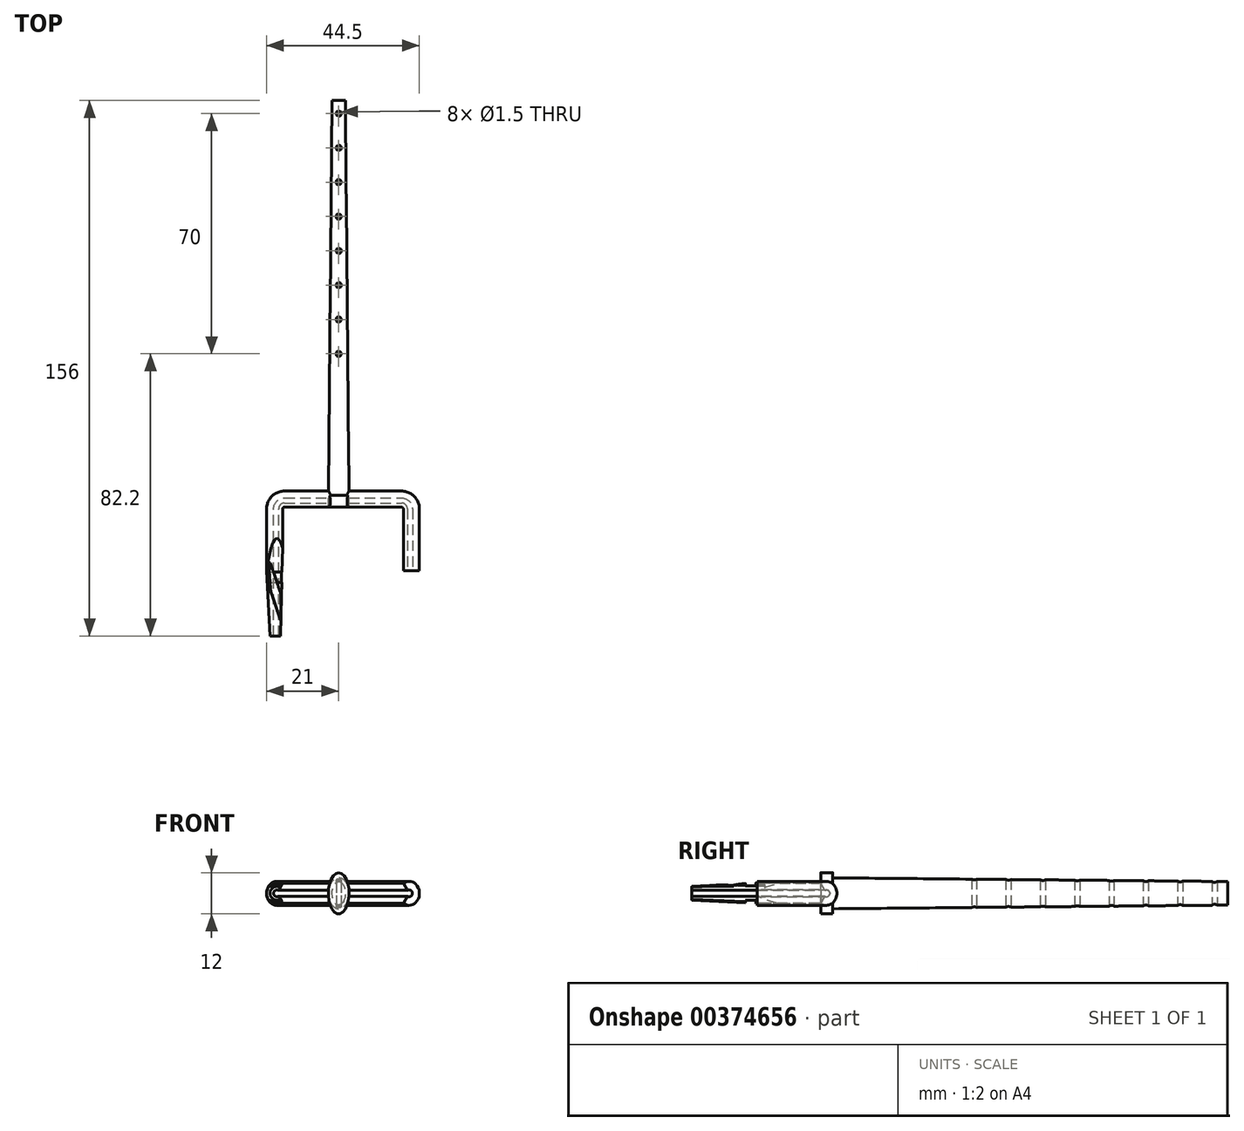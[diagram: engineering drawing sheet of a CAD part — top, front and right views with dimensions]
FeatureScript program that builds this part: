
annotation { "Feature Type Name" : "Feature", "Feature Type Description" : "" }
export const myFeature = defineFeature(function(context is Context, id is Id, definition is map)
    precondition{}
    {
        {
            var Q0;
            Q0=qCreatedBy(makeId("Front.planeOp"),FACE);
            var sketch = newSketch(context, id + "F0", { "sketchPlane" : qUnion([Q0])});
            skArc(sketch, "E0", {"start": v(0.49, 0.84) * mm, "mid": v(-0.97, 0) * mm, "end": v(0.49, -0.84) * mm});
            skLineSegment(sketch, "E1", {"start": v(0.49, 0.84) * mm, "end": v(1.68, 2.9) * mm});
            skLineSegment(sketch, "E2", {"start": v(0.49, -0.84) * mm, "end": v(1.68, -2.9) * mm});
            skEllipticalArc(sketch, "E3", {});
            const initialGuessF0  = {"E3": [0, 0, -1, 0, 0.003, 0.0035, 4.1196187055742195, 2.1635666016053645]};
            skSetInitialGuess(sketch, initialGuessF0);
            skSolve(sketch);
        }
        {
            var Q0;
            Q0=qCreatedBy(makeId("Top.planeOp"),FACE);
            var sketch = newSketch(context, id + "F1", { "sketchPlane" : qUnion([Q0])});
            skLineSegment(sketch, "E4", {"start": v(0, 0) * mm, "end": v(0, 37) * mm});
            skArc(sketch, "E5", {"start": v(0, 37) * mm, "mid": v(0.64, 38.56) * mm, "end": v(2.2, 39.2) * mm});
            skLineSegment(sketch, "E6", {"start": v(2.2, 39.2) * mm, "end": v(36.3, 39.2) * mm});
            skArc(sketch, "E7", {"start": v(38.5, 37) * mm, "mid": v(37.86, 38.56) * mm, "end": v(36.3, 39.2) * mm});
            skLineSegment(sketch, "E8", {"start": v(38.5, 37) * mm, "end": v(38.5, 19) * mm});
            skSolve(sketch);
        }
        {
            var Q0;
            Q0=qSketchRegion(id+"F0",true);
            var Q1;
            Q1=qConstructionFilter(qBodyType(qCreatedBy(id+"F0",EDGE),BodyType.WIRE),ConstructionObject.NO);
            var Q2;
            Q2=qConstructionFilter(qBodyType(qCreatedBy(id+"F1",EDGE),BodyType.WIRE),ConstructionObject.NO);
            sweep(context, id + "F2", {"profiles" : qUnion([Q0]), "surfaceProfiles" : qUnion([Q1]), "path" : qUnion([Q2])});
        }
        {
            var Q0;
            Q0=qCreatedBy(makeId("Right.planeOp"),FACE);
            var sketch = newSketch(context, id + "F3", { "sketchPlane" : qUnion([Q0])});
            skLineSegment(sketch, "E9", {"start": v(0, 2) * mm, "end": v(28.41, 3.5) * mm});
            skLineSegment(sketch, "E10", {"start": v(-1.87, 2) * mm, "end": v(0, 2) * mm});
            skLineSegment(sketch, "E11", {"start": v(-4.03, 0) * mm, "end": v(22.25, 0) * mm, "construction": true});
            skLineSegment(sketch, "E12", {"start": v(28.41, 3.5) * mm, "end": v(28.41, 8.2) * mm});
            skLineSegment(sketch, "E13", {"start": v(28.41, 8.2) * mm, "end": v(-1.87, 8.2) * mm});
            skLineSegment(sketch, "E14", {"start": v(-1.87, 8.2) * mm, "end": v(-1.87, 2) * mm});
            skSolve(sketch);
        }
        {
            var Q0;
            Q0=makeQuery(id+"F3.imprint","IMPRINT",FACE,{"disambiguationData":[TD([[makeQuery(id+"F3.imprint","IMPRINT",EDGE,{"derivedFrom":sQuery(id+"F3.wireOp",EDGE,"E9")}),1.0]])]});
            var Q1;
            Q1=sQuery(id+"F3.wireOp",EDGE,"E11");
            revolve(context, id + "F4", {"operationType" : NewBodyOperationType.REMOVE, "entities" : qUnion([Q0]), "axis" : qUnion([Q1]), "revolveType" : RevolveType.FULL, "oppositeDirection" : true});
        }
        {
            var Q0;
            Q0=qCreatedBy(makeId("Top.planeOp"),FACE);
            cPlane(context, id + "F5", {"entities" : qUnion([Q0]), "cplaneType" : CPlaneType.OFFSET, "offset" : 10 * mm, "width" : 150 * mm, "height" : 150 * mm});
        }
        {
            var Q0;
            Q0=qCreatedBy(id+"F5.planeOp",FACE);
            var sketch = newSketch(context, id + "F6", { "sketchPlane" : qUnion([Q0])});
            skLineSegment(sketch, "E15", {"start": v(1.23, 4) * mm, "end": v(-4.27, 20.45) * mm});
            skLineSegment(sketch, "E16", {"start": v(-4.27, 20.45) * mm, "end": v(-1.9, 21.25) * mm});
            skLineSegment(sketch, "E17", {"start": v(-1.9, 21.25) * mm, "end": v(3.75, 4.36) * mm});
            skLineSegment(sketch, "E18", {"start": v(3.75, 4.36) * mm, "end": v(1.23, 4) * mm});
            skLineSegment(sketch, "E19", {"start": v(-4.35, 16) * mm, "end": v(7.78, 16) * mm, "construction": true});
            skLineSegment(sketch, "E20", {"start": v(-5.1, 4) * mm, "end": v(7.56, 4) * mm, "construction": true});
            skSolve(sketch);
        }
        {
            var Q0;
            Q0 = qSketchRegion(id + "F6", true);
            extrude(context, id + "F7", {"entities" : qUnion([Q0]), "operationType" : NewBodyOperationType.REMOVE, "oppositeDirection" : true, "depth" : 8 * mm, "offsetDistance" : 25 * mm});
        }
        {
            var Q0;
            Q0=qCreatedBy(makeId("Right.planeOp"),FACE);
            var sketch = newSketch(context, id + "F8", { "sketchPlane" : qUnion([Q0])});
            skLineSegment(sketch, "E21.bottom", {"start": v(15.6, 2.23) * mm, "end": v(18.6, 2.23) * mm});
            skLineSegment(sketch, "E21.top", {"start": v(15.6, 4.52) * mm, "end": v(18.6, 4.52) * mm});
            skLineSegment(sketch, "E21.left", {"start": v(15.6, 2.23) * mm, "end": v(15.6, 4.52) * mm});
            skLineSegment(sketch, "E21.right", {"start": v(18.6, 2.23) * mm, "end": v(18.6, 4.52) * mm});
            skLineSegment(sketch, "E22.bottom", {"start": v(15.6, -2.04) * mm, "end": v(18.6, -2.04) * mm});
            skLineSegment(sketch, "E22.top", {"start": v(15.6, -3.78) * mm, "end": v(18.6, -3.78) * mm});
            skLineSegment(sketch, "E22.left", {"start": v(15.6, -2.04) * mm, "end": v(15.6, -3.78) * mm});
            skLineSegment(sketch, "E22.right", {"start": v(18.6, -2.04) * mm, "end": v(18.6, -3.78) * mm});
            skSolve(sketch);
        }
        {
            var Q0;
            Q0 = qSketchRegion(id + "F8", true);
            extrude(context, id + "F9", {"entities" : qUnion([Q0]), "operationType" : NewBodyOperationType.REMOVE, "oppositeDirection" : true, "depth" : 3 * mm, "offsetDistance" : 25 * mm, "hasSecondDirection" : true, "secondDirectionOppositeDirection" : false, "secondDirectionDepth" : 5 * mm});
        }
        {
            var Q0;
            Q0=makeQuery(id+"F2.opSweep","CAP_FACE",FACE,{"disambiguationData":[OSD([sQuery(id+"F0.wireOp",EDGE,"E0"),sQuery(id+"F0.wireOp",EDGE,"E1"),sQuery(id+"F0.wireOp",EDGE,"E2"),sQuery(id+"F0.wireOp",EDGE,"E3"),sQuery(id+"F1.wireOp",VERTEX,"E8.end")])],"isStart":false});
            cPlane(context, id + "F10", {"entities" : qUnion([Q0]), "cplaneType" : CPlaneType.OFFSET, "offset" : 22 * mm, "oppositeDirection" : true, "width" : 150 * mm, "height" : 150 * mm});
        }
        {
            var Q0;
            Q0=qCreatedBy(id+"F10.planeOp",FACE);
            var sketch = newSketch(context, id + "F11", { "sketchPlane" : qUnion([Q0])});
            skEllipse(sketch, "E23", {"center": v(18, 0) * mm, "majorRadius": 4.5 * mm, "minorRadius": 3 * mm, "majorAxis": v(0, -1)});
            skSolve(sketch);
        }
        {
            var Q0;
            Q0 = qSketchRegion(id + "F11", true);
            extrude(context, id + "F12", {"entities" : qUnion([Q0]), "operationType" : NewBodyOperationType.ADD, "oppositeDirection" : true, "depth" : 115 * mm, "offsetDistance" : 25 * mm, "hasDraft" : true, "draftAngle" : 0.53 * degree, "draftPullDirection" : true});
        }
        {
            var Q0;
            Q0=makeQuery(id+"F12.boolean.opBoolean","SPLIT",FACE,{"disambiguationData":[OD(1.0)],"derivedFrom":makeQuery(id+"F12.opExtrude","CAP_FACE",FACE,{"disambiguationData":[OSD([sQuery(id+"F11.wireOp",EDGE,"E23")])],"isStart":true})});
            var sketch = newSketch(context, id + "F13", { "sketchPlane" : qUnion([Q0])});
            skFitSpline(sketch, "E24.0.0", {"points": [v(18, 6) * mm, v(17.8, 6) * mm, v(17.6, 5.96) * mm, v(17.22, 5.8) * mm, v(17.03, 5.7) * mm, v(16.67, 5.4) * mm, v(16.5, 5.2) * mm, v(16.17, 4.77) * mm, v(16.02, 4.52) * mm, v(15.74, 3.96) * mm, v(15.61, 3.66) * mm, v(15.4, 3) * mm, v(15.3, 2.66) * mm, v(15.08, 1.57) * mm, v(15, 0.79) * mm, v(15, -0.79) * mm, v(15.08, -1.57) * mm, v(15.3, -2.66) * mm, v(15.4, -3) * mm, v(15.61, -3.66) * mm, v(15.74, -3.96) * mm, v(16.02, -4.52) * mm, v(16.17, -4.77) * mm, v(16.5, -5.2) * mm, v(16.67, -5.4) * mm, v(17.03, -5.7) * mm, v(17.22, -5.8) * mm, v(17.6, -5.96) * mm, v(17.8, -6) * mm, v(18, -6) * mm, v(18.2, -6) * mm, v(18.4, -5.96) * mm, v(18.78, -5.8) * mm, v(18.97, -5.7) * mm, v(19.33, -5.4) * mm, v(19.5, -5.2) * mm, v(19.83, -4.77) * mm, v(19.98, -4.52) * mm, v(20.26, -3.96) * mm, v(20.39, -3.66) * mm, v(20.6, -3) * mm, v(20.7, -2.66) * mm, v(20.92, -1.57) * mm, v(21, -0.79) * mm, v(21, 0.79) * mm, v(20.92, 1.57) * mm, v(20.7, 2.66) * mm, v(20.6, 3) * mm, v(20.39, 3.66) * mm, v(20.26, 3.96) * mm, v(19.98, 4.52) * mm, v(19.83, 4.77) * mm, v(19.5, 5.2) * mm, v(19.33, 5.4) * mm, v(18.97, 5.7) * mm, v(18.78, 5.8) * mm, v(18.4, 5.96) * mm, v(18.2, 6) * mm, v(18, 6) * mm]});
            skLineSegment(sketch, "E24.0.1", {"start": v(15.65, 2.8) * mm, "end": v(20.35, 2.8) * mm});
            skFitSpline(sketch, "E25.0.0", {"points": [v(18, 6) * mm, v(17.8, 6) * mm, v(17.6, 5.96) * mm, v(17.22, 5.8) * mm, v(17.03, 5.7) * mm, v(16.67, 5.4) * mm, v(16.5, 5.2) * mm, v(16.17, 4.77) * mm, v(16.02, 4.52) * mm, v(15.74, 3.96) * mm, v(15.61, 3.66) * mm, v(15.4, 3) * mm, v(15.3, 2.66) * mm, v(15.08, 1.57) * mm, v(15, 0.79) * mm, v(15, -0.79) * mm, v(15.08, -1.57) * mm, v(15.3, -2.66) * mm, v(15.4, -3) * mm, v(15.61, -3.66) * mm, v(15.74, -3.96) * mm, v(16.02, -4.52) * mm, v(16.17, -4.77) * mm, v(16.5, -5.2) * mm, v(16.67, -5.4) * mm, v(17.03, -5.7) * mm, v(17.22, -5.8) * mm, v(17.6, -5.96) * mm, v(17.8, -6) * mm, v(18, -6) * mm, v(18.2, -6) * mm, v(18.4, -5.96) * mm, v(18.78, -5.8) * mm, v(18.97, -5.7) * mm, v(19.33, -5.4) * mm, v(19.5, -5.2) * mm, v(19.83, -4.77) * mm, v(19.98, -4.52) * mm, v(20.26, -3.96) * mm, v(20.39, -3.66) * mm, v(20.6, -3) * mm, v(20.7, -2.66) * mm, v(20.92, -1.57) * mm, v(21, -0.79) * mm, v(21, 0.79) * mm, v(20.92, 1.57) * mm, v(20.7, 2.66) * mm, v(20.6, 3) * mm, v(20.39, 3.66) * mm, v(20.26, 3.96) * mm, v(19.98, 4.52) * mm, v(19.83, 4.77) * mm, v(19.5, 5.2) * mm, v(19.33, 5.4) * mm, v(18.97, 5.7) * mm, v(18.78, 5.8) * mm, v(18.4, 5.96) * mm, v(18.2, 6) * mm, v(18, 6) * mm]});
            skLineSegment(sketch, "E25.0.1", {"start": v(20.35, -2.8) * mm, "end": v(15.65, -2.8) * mm});
            skSolve(sketch);
        }
        {
            var Q0;
            Q0 = qSketchRegion(id + "F13", true);
            extrude(context, id + "F14", {"entities" : qUnion([Q0]), "operationType" : NewBodyOperationType.ADD, "depth" : 3.5 * mm, "offsetDistance" : 25 * mm});
        }
        {
            var Q0;
            Q0=qCreatedBy(makeId("Top.planeOp"),FACE);
            var sketch = newSketch(context, id + "F15", { "sketchPlane" : qUnion([Q0])});
            skLineSegment(sketch, "E26", {"start": v(18, 36.53) * mm, "end": v(18, 48.98) * mm, "construction": true});
            skCircle(sketch, "E27", {"center": v(18, 152.2) * mm, "radius": 0.75 * mm});
            skCircle(sketch, "E28.0.1.0", {"center": v(18, 142.2) * mm, "radius": 0.75 * mm});
            skCircle(sketch, "E28.0.2.0", {"center": v(18, 132.2) * mm, "radius": 0.75 * mm});
            skCircle(sketch, "E28.0.3.0", {"center": v(18, 122.2) * mm, "radius": 0.75 * mm});
            skCircle(sketch, "E28.0.4.0", {"center": v(18, 112.2) * mm, "radius": 0.75 * mm});
            skCircle(sketch, "E28.0.5.0", {"center": v(18, 102.2) * mm, "radius": 0.75 * mm});
            skCircle(sketch, "E28.0.6.0", {"center": v(18, 92.2) * mm, "radius": 0.75 * mm});
            skCircle(sketch, "E28.0.7.0", {"center": v(18, 82.2) * mm, "radius": 0.75 * mm});
            skLineSegment(sketch, "E28.direction1", {"start": v(18, 152.2) * mm, "end": v(-7, 152.2) * mm, "construction": true});
            skLineSegment(sketch, "E28.direction2", {"start": v(18, 152.2) * mm, "end": v(18, 142.2) * mm, "construction": true});
            skSolve(sketch);
        }
        {
            var Q0;
            Q0 = qSketchRegion(id + "F15", true);
            extrude(context, id + "F16", {"entities" : qUnion([Q0]), "operationType" : NewBodyOperationType.REMOVE, "endBound" : BoundingType.THROUGH_ALL, "depth" : 25 * mm, "offsetDistance" : 25 * mm});
        }
        {
            var Q0;
            Q0 = qSketchRegion(id + "F15", true);
            extrude(context, id + "F17", {"entities" : qUnion([Q0]), "operationType" : NewBodyOperationType.REMOVE, "oppositeDirection" : true, "depth" : 25 * mm, "offsetDistance" : 25 * mm});
        }
    });
